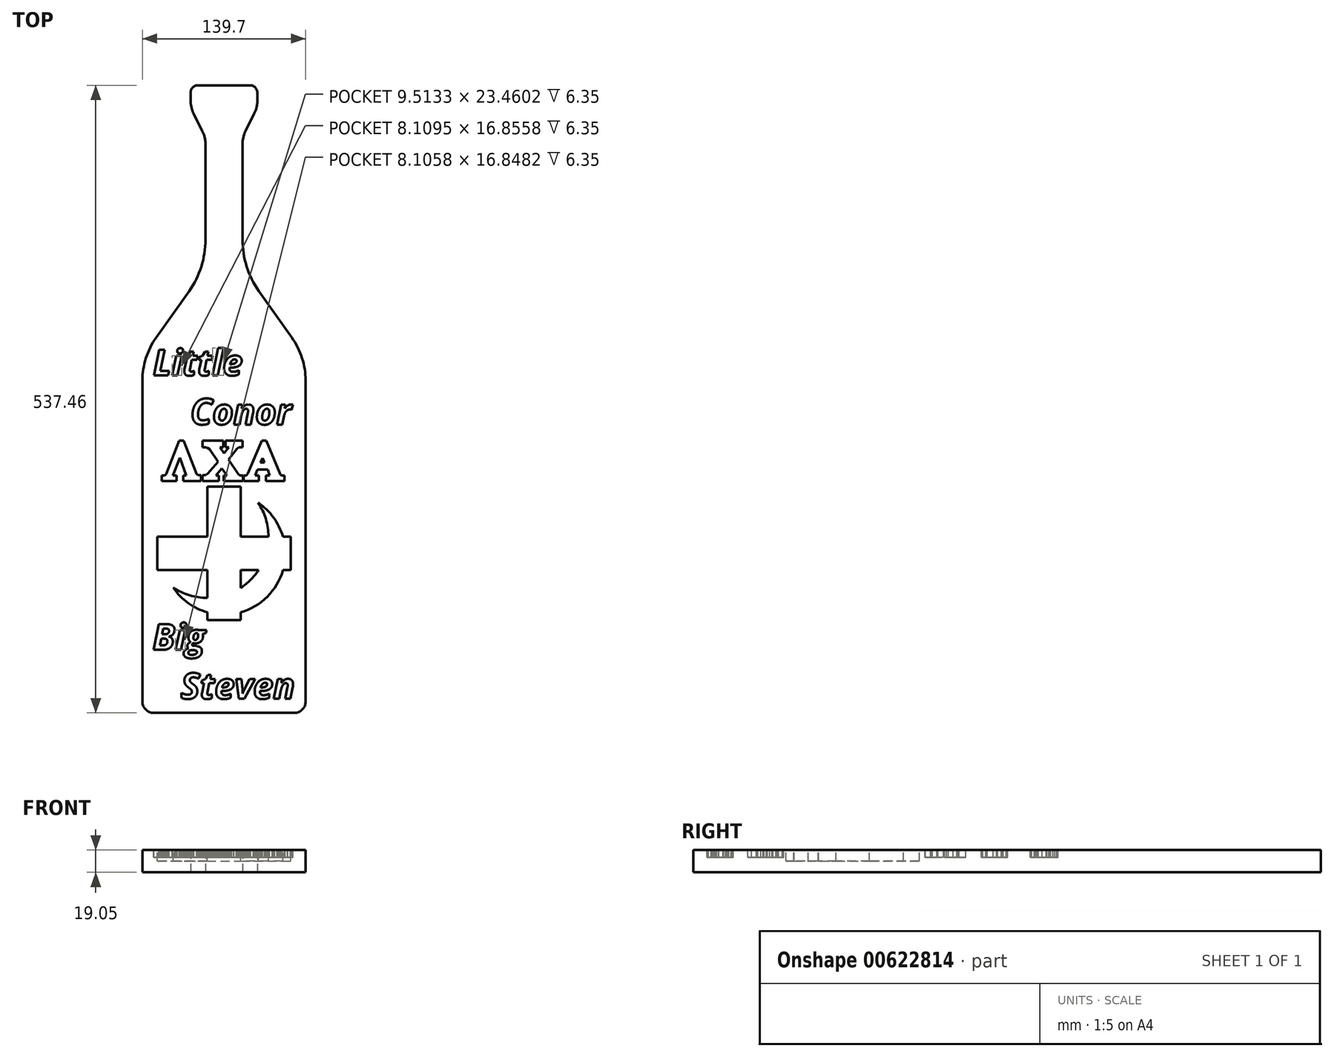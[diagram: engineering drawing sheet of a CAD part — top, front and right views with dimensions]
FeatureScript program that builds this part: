
annotation { "Feature Type Name" : "Feature", "Feature Type Description" : "" }
export const myFeature = defineFeature(function(context is Context, id is Id, definition is map)
    precondition{}
    {
        {
            var Q0;
            Q0=qCreatedBy(makeId("Top.planeOp"),FACE);
            var sketch = newSketch(context, id + "F0", { "sketchPlane" : qUnion([Q0])});
            skLineSegment(sketch, "E0", {"start": v(0, 0) * mm, "end": v(60.33, 0) * mm});
            skLineSegment(sketch, "E1", {"start": v(69.85, 9.53) * mm, "end": v(69.85, 284.59) * mm});
            skLineSegment(sketch, "E2", {"start": v(58.17, 321.3) * mm, "end": v(29.9, 361.2) * mm});
            skLineSegment(sketch, "E3", {"start": v(15.87, 405.25) * mm, "end": v(15.87, 487.01) * mm});
            skLineSegment(sketch, "E4", {"start": v(18.56, 498.37) * mm, "end": v(25.9, 513.04) * mm});
            skLineSegment(sketch, "E5", {"start": v(28.57, 524.4) * mm, "end": v(28.57, 531.1) * mm});
            skLineSegment(sketch, "E6", {"start": v(22.22, 537.46) * mm, "end": v(0, 537.46) * mm});
            skLineSegment(sketch, "E7", {"start": v(0, 537.46) * mm, "end": v(0, 0) * mm});
            skPoint(sketch, "E8.visualSharp", {"position": v(28.57, 537.46) * mm});
            skArc(sketch, "E8.filletArc", {"start": v(28.57, 531.1) * mm, "mid": v(26.72, 535.6) * mm, "end": v(22.22, 537.46) * mm});
            skPoint(sketch, "E9.visualSharp", {"position": v(28.57, 518.4) * mm});
            skArc(sketch, "E9.filletArc", {"start": v(25.9, 513.04) * mm, "mid": v(27.9, 518.57) * mm, "end": v(28.57, 524.4) * mm});
            skPoint(sketch, "E10.visualSharp", {"position": v(15.88, 493) * mm});
            skArc(sketch, "E10.filletArc", {"start": v(18.56, 498.37) * mm, "mid": v(16.55, 492.85) * mm, "end": v(15.87, 487.01) * mm});
            skPoint(sketch, "E11.visualSharp", {"position": v(15.87, 381) * mm});
            skArc(sketch, "E11.filletArc", {"start": v(15.87, 405.25) * mm, "mid": v(19.46, 382.14) * mm, "end": v(29.9, 361.2) * mm});
            skPoint(sketch, "E12.visualSharp", {"position": v(69.85, 304.8) * mm});
            skArc(sketch, "E12.filletArc", {"start": v(69.85, 284.59) * mm, "mid": v(66.86, 303.85) * mm, "end": v(58.17, 321.3) * mm});
            skPoint(sketch, "E13.visualSharp", {"position": v(69.85, 0) * mm});
            skArc(sketch, "E13.filletArc", {"start": v(60.33, 0) * mm, "mid": v(67.06, 2.79) * mm, "end": v(69.85, 9.53) * mm});
            skArc(sketch, "E14.MirrorCS", {"start": v(-25.9, 513.04) * mm, "mid": v(-27.9, 518.57) * mm, "end": v(-28.57, 524.4) * mm});
            skLineSegment(sketch, "E15.MirrorCS", {"start": v(-28.57, 524.4) * mm, "end": v(-28.57, 531.1) * mm});
            skArc(sketch, "E16.MirrorCS", {"start": v(-28.57, 531.1) * mm, "mid": v(-26.72, 535.6) * mm, "end": v(-22.22, 537.46) * mm});
            skArc(sketch, "E17.MirrorCS", {"start": v(-18.56, 498.37) * mm, "mid": v(-16.55, 492.85) * mm, "end": v(-15.87, 487.01) * mm});
            skArc(sketch, "E18.MirrorCS", {"start": v(-60.33, 0) * mm, "mid": v(-67.06, 2.79) * mm, "end": v(-69.85, 9.53) * mm});
            skLineSegment(sketch, "E19.MirrorCS", {"start": v(-18.56, 498.37) * mm, "end": v(-25.9, 513.04) * mm});
            skArc(sketch, "E20.MirrorCS", {"start": v(-69.85, 284.59) * mm, "mid": v(-66.86, 303.85) * mm, "end": v(-58.17, 321.3) * mm});
            skPoint(sketch, "E21.MirrorP", {"position": v(-69.85, 0) * mm});
            skLineSegment(sketch, "E22.MirrorCS", {"start": v(-69.85, 9.53) * mm, "end": v(-69.85, 284.59) * mm});
            skLineSegment(sketch, "E23.MirrorCS", {"start": v(-58.17, 321.3) * mm, "end": v(-29.9, 361.2) * mm});
            skLineSegment(sketch, "E24.MirrorCS", {"start": v(-15.87, 405.25) * mm, "end": v(-15.87, 487.01) * mm});
            skPoint(sketch, "E25.MirrorP", {"position": v(-69.85, 304.8) * mm});
            skPoint(sketch, "E26.MirrorP", {"position": v(-15.87, 381) * mm});
            skPoint(sketch, "E27.MirrorP", {"position": v(-28.57, 537.46) * mm});
            skArc(sketch, "E28.MirrorCS", {"start": v(-15.87, 405.25) * mm, "mid": v(-19.46, 382.14) * mm, "end": v(-29.9, 361.2) * mm});
            skPoint(sketch, "E29.MirrorP", {"position": v(-15.88, 493) * mm});
            skPoint(sketch, "E30.MirrorP", {"position": v(-28.57, 518.4) * mm});
            skLineSegment(sketch, "E31.MirrorCS", {"start": v(0, 0) * mm, "end": v(-60.33, 0) * mm});
            skLineSegment(sketch, "E32.MirrorCS", {"start": v(-22.22, 537.46) * mm, "end": v(0, 537.46) * mm});
            skSolve(sketch);
        }
        {
            var Q0;
            Q0 = qSketchRegion(id + "F0", true);
            extrude(context, id + "F1", {"entities" : qUnion([Q0]), "depth" : 19.05 * mm, "offsetDistance" : 25.4 * mm});
        }
        {
            var Q0;
            Q0=makeQuery(id+"F1.opExtrude","CAP_FACE",FACE,{"disambiguationData":[OSD([sQuery(id+"F0.wireOp",EDGE,"E0"),sQuery(id+"F0.wireOp",EDGE,"E1"),sQuery(id+"F0.wireOp",EDGE,"E2"),sQuery(id+"F0.wireOp",EDGE,"E3"),sQuery(id+"F0.wireOp",EDGE,"E4"),sQuery(id+"F0.wireOp",EDGE,"E5"),sQuery(id+"F0.wireOp",EDGE,"E6"),sQuery(id+"F0.wireOp",EDGE,"E8.filletArc"),sQuery(id+"F0.wireOp",EDGE,"E9.filletArc"),sQuery(id+"F0.wireOp",EDGE,"E10.filletArc"),sQuery(id+"F0.wireOp",EDGE,"E11.filletArc"),sQuery(id+"F0.wireOp",EDGE,"E12.filletArc"),sQuery(id+"F0.wireOp",EDGE,"E13.filletArc"),sQuery(id+"F0.wireOp",EDGE,"E14.MirrorCS"),sQuery(id+"F0.wireOp",EDGE,"E15.MirrorCS"),sQuery(id+"F0.wireOp",EDGE,"E16.MirrorCS"),sQuery(id+"F0.wireOp",EDGE,"E17.MirrorCS"),sQuery(id+"F0.wireOp",EDGE,"E18.MirrorCS"),sQuery(id+"F0.wireOp",EDGE,"E19.MirrorCS"),sQuery(id+"F0.wireOp",EDGE,"E20.MirrorCS"),sQuery(id+"F0.wireOp",EDGE,"E22.MirrorCS"),sQuery(id+"F0.wireOp",EDGE,"E23.MirrorCS"),sQuery(id+"F0.wireOp",EDGE,"E24.MirrorCS"),sQuery(id+"F0.wireOp",EDGE,"E28.MirrorCS"),sQuery(id+"F0.wireOp",EDGE,"E31.MirrorCS"),sQuery(id+"F0.wireOp",EDGE,"E32.MirrorCS")])],"isStart":false});
            var sketch = newSketch(context, id + "F2", { "sketchPlane" : qUnion([Q0])});
            skText(sketch, "E33", { "text": "Little \n    Conor", "fontName": "OpenSans-BoldItalic.ttf"});
            const initialGuessF2  = {"E33": [-0.06094, 0.28892, 1, 0, 0.02223]};
            skSetInitialGuess(sketch, initialGuessF2);
            skSolve(sketch);
        }
        {
            var Q0;
            Q0 = qSketchRegion(id + "F2", true);
            extrude(context, id + "F3", {"entities" : qUnion([Q0]), "operationType" : NewBodyOperationType.REMOVE, "oppositeDirection" : true, "depth" : 6.35 * mm, "offsetDistance" : 25.4 * mm});
        }
        {
            var Q0;
            {var subQ0=sQuery(id+"F0.wireOp",EDGE,"E23.MirrorCS");var subQ1=sQuery(id+"F0.wireOp",EDGE,"E22.MirrorCS");var subQ2=sQuery(id+"F0.wireOp",EDGE,"E20.MirrorCS");var subQ3=sQuery(id+"F0.wireOp",EDGE,"E19.MirrorCS");var subQ4=sQuery(id+"F0.wireOp",EDGE,"E18.MirrorCS");var subQ5=sQuery(id+"F0.wireOp",EDGE,"E17.MirrorCS");var subQ6=sQuery(id+"F0.wireOp",EDGE,"E16.MirrorCS");var subQ7=sQuery(id+"F0.wireOp",EDGE,"E15.MirrorCS");var subQ8=sQuery(id+"F0.wireOp",EDGE,"E14.MirrorCS");var subQ9=sQuery(id+"F0.wireOp",EDGE,"E13.filletArc");var subQ10=sQuery(id+"F0.wireOp",EDGE,"E12.filletArc");var subQ11=sQuery(id+"F0.wireOp",EDGE,"E11.filletArc");var subQ12=sQuery(id+"F0.wireOp",EDGE,"E3");var subQ13=sQuery(id+"F0.wireOp",EDGE,"E2");var subQ14=sQuery(id+"F0.wireOp",EDGE,"E1");var subQ15=sQuery(id+"F0.wireOp",EDGE,"E31.MirrorCS");var subQ16=sQuery(id+"F0.wireOp",EDGE,"E0");var subQ17=sQuery(id+"F0.wireOp",EDGE,"E4");var subQ18=sQuery(id+"F0.wireOp",EDGE,"E5");var subQ19=sQuery(id+"F0.wireOp",EDGE,"E32.MirrorCS");var subQ20=sQuery(id+"F0.wireOp",EDGE,"E6");var subQ21=sQuery(id+"F0.wireOp",EDGE,"E8.filletArc");var subQ22=sQuery(id+"F0.wireOp",EDGE,"E9.filletArc");var subQ23=sQuery(id+"F0.wireOp",EDGE,"E10.filletArc");var subQ24=sQuery(id+"F0.wireOp",EDGE,"E24.MirrorCS");var subQ25=sQuery(id+"F0.wireOp",EDGE,"E28.MirrorCS");Q0=makeQuery(id+"F3.boolean.opBoolean","SPLIT",FACE,{"disambiguationData":[TD([makeQuery(id+"F1.opExtrude","SWEPT_FACE",FACE,{"disambiguationData":[OSD([subQ14])]})])],"derivedFrom":makeQuery(id+"F1.opExtrude","CAP_FACE",FACE,{"disambiguationData":[OSD([subQ16,subQ14,subQ13,subQ12,subQ17,subQ18,subQ20,subQ21,subQ22,subQ23,subQ11,subQ10,subQ9,subQ8,subQ7,subQ6,subQ5,subQ4,subQ3,subQ2,subQ1,subQ0,subQ24,subQ25,subQ15,subQ19])],"isStart":false})});}
            var sketch = newSketch(context, id + "F4", { "sketchPlane" : qUnion([Q0])});
            skText(sketch, "E34", { "text": "Big\n   Steven", "fontName": "OpenSans-BoldItalic.ttf"});
            const initialGuessF4  = {"E34": [-0.06118, 0.05398, 1, 0, 0.02222]};
            skSetInitialGuess(sketch, initialGuessF4);
            skSolve(sketch);
        }
        {
            var Q0;
            Q0 = qSketchRegion(id + "F4", true);
            extrude(context, id + "F5", {"entities" : qUnion([Q0]), "operationType" : NewBodyOperationType.REMOVE, "oppositeDirection" : true, "depth" : 6.35 * mm, "offsetDistance" : 25.4 * mm});
        }
        {
            var Q0;
            {var subQ67=sQuery(id+"F0.wireOp",EDGE,"E28.MirrorCS");var subQ69=sQuery(id+"F0.wireOp",EDGE,"E24.MirrorCS");var subQ72=sQuery(id+"F0.wireOp",EDGE,"E10.filletArc");var subQ76=sQuery(id+"F0.wireOp",EDGE,"E9.filletArc");var subQ81=sQuery(id+"F0.wireOp",EDGE,"E8.filletArc");var subQ86=sQuery(id+"F0.wireOp",EDGE,"E32.MirrorCS");var subQ87=sQuery(id+"F0.wireOp",EDGE,"E6");var subQ92=sQuery(id+"F0.wireOp",EDGE,"E5");var subQ97=sQuery(id+"F0.wireOp",EDGE,"E4");var subQ102=sQuery(id+"F0.wireOp",EDGE,"E31.MirrorCS");var subQ103=sQuery(id+"F0.wireOp",EDGE,"E0");var subQ107=sQuery(id+"F0.wireOp",EDGE,"E1");var subQ108=makeQuery(id+"F1.opExtrude","SWEPT_FACE",FACE,{"disambiguationData":[OSD([subQ107])]});var subQ111=sQuery(id+"F0.wireOp",EDGE,"E2");var subQ114=sQuery(id+"F0.wireOp",EDGE,"E3");var subQ117=sQuery(id+"F0.wireOp",EDGE,"E11.filletArc");var subQ121=sQuery(id+"F0.wireOp",EDGE,"E12.filletArc");var subQ125=sQuery(id+"F0.wireOp",EDGE,"E13.filletArc");var subQ129=sQuery(id+"F0.wireOp",EDGE,"E14.MirrorCS");var subQ133=sQuery(id+"F0.wireOp",EDGE,"E15.MirrorCS");var subQ136=sQuery(id+"F0.wireOp",EDGE,"E16.MirrorCS");var subQ140=sQuery(id+"F0.wireOp",EDGE,"E17.MirrorCS");var subQ143=sQuery(id+"F0.wireOp",EDGE,"E18.MirrorCS");var subQ146=sQuery(id+"F0.wireOp",EDGE,"E19.MirrorCS");var subQ149=sQuery(id+"F0.wireOp",EDGE,"E20.MirrorCS");var subQ152=sQuery(id+"F0.wireOp",EDGE,"E22.MirrorCS");var subQ155=sQuery(id+"F0.wireOp",EDGE,"E23.MirrorCS");Q0=makeQuery(id+"F5.boolean.opBoolean","SPLIT",FACE,{"disambiguationData":[TD([subQ108])],"derivedFrom":makeQuery(id+"F3.boolean.opBoolean","SPLIT",FACE,{"disambiguationData":[TD([subQ108])],"derivedFrom":makeQuery(id+"F1.opExtrude","CAP_FACE",FACE,{"disambiguationData":[OSD([subQ103,subQ107,subQ111,subQ114,subQ97,subQ92,subQ87,subQ81,subQ76,subQ72,subQ117,subQ121,subQ125,subQ129,subQ133,subQ136,subQ140,subQ143,subQ146,subQ149,subQ152,subQ155,subQ69,subQ67,subQ102,subQ86])],"isStart":false})})});}
            var sketch = newSketch(context, id + "F6", { "sketchPlane" : qUnion([Q0])});
            skLineSegment(sketch, "E35", {"start": v(-38.42, 233.14) * mm, "end": v(-34.63, 233.14) * mm});
            skLineSegment(sketch, "E36", {"start": v(-34.63, 233.14) * mm, "end": v(-23.55, 204.57) * mm});
            skLineSegment(sketch, "E37", {"start": v(-23.55, 204.57) * mm, "end": v(-22.06, 203.69) * mm});
            skLineSegment(sketch, "E38", {"start": v(-22.06, 203.69) * mm, "end": v(-19.65, 203.69) * mm});
            skLineSegment(sketch, "E39", {"start": v(-19.65, 203.69) * mm, "end": v(-19.65, 198.54) * mm});
            skLineSegment(sketch, "E40", {"start": v(-19.65, 198.54) * mm, "end": v(-34.88, 198.54) * mm});
            skLineSegment(sketch, "E41", {"start": v(-34.88, 198.54) * mm, "end": v(-34.88, 203.37) * mm});
            skLineSegment(sketch, "E42", {"start": v(-34.88, 203.37) * mm, "end": v(-32.33, 203.37) * mm});
            skLineSegment(sketch, "E43", {"start": v(-32.33, 203.37) * mm, "end": v(-37.72, 218.5) * mm});
            skLineSegment(sketch, "E44", {"start": v(-37.72, 218.5) * mm, "end": v(-43.75, 203.37) * mm});
            skLineSegment(sketch, "E45", {"start": v(-43.75, 203.37) * mm, "end": v(-40.53, 203.37) * mm});
            skLineSegment(sketch, "E46", {"start": v(-40.53, 203.37) * mm, "end": v(-40.53, 198.64) * mm});
            skLineSegment(sketch, "E47", {"start": v(-40.53, 198.64) * mm, "end": v(-53.42, 198.64) * mm});
            skLineSegment(sketch, "E48", {"start": v(-53.42, 198.64) * mm, "end": v(-53.42, 203.37) * mm});
            skLineSegment(sketch, "E49", {"start": v(-53.42, 203.37) * mm, "end": v(-50.8, 203.37) * mm});
            skLineSegment(sketch, "E50", {"start": v(-50.8, 203.37) * mm, "end": v(-49.64, 204.6) * mm});
            skLineSegment(sketch, "E51", {"start": v(-49.64, 204.6) * mm, "end": v(-38.42, 233.14) * mm});
            skLineSegment(sketch, "E52", {"start": v(-18.45, 198.54) * mm, "end": v(-18.45, 203.69) * mm});
            skLineSegment(sketch, "E53", {"start": v(-18.45, 203.69) * mm, "end": v(-15.83, 203.69) * mm});
            skLineSegment(sketch, "E54", {"start": v(-15.83, 203.69) * mm, "end": v(-14, 204.75) * mm});
            skLineSegment(sketch, "E55", {"start": v(-14, 204.75) * mm, "end": v(-5.2, 215.13) * mm});
            skLineSegment(sketch, "E56", {"start": v(-5.2, 215.13) * mm, "end": v(-12.52, 225.7) * mm});
            skLineSegment(sketch, "E57", {"start": v(-12.52, 225.7) * mm, "end": v(-13.87, 226.8) * mm});
            skLineSegment(sketch, "E58", {"start": v(-13.87, 226.8) * mm, "end": v(-15.79, 227.45) * mm});
            skLineSegment(sketch, "E59", {"start": v(-15.79, 227.45) * mm, "end": v(-18.45, 227.45) * mm});
            skLineSegment(sketch, "E60", {"start": v(-0.48, 227.45) * mm, "end": v(-3.46, 227.45) * mm});
            skLineSegment(sketch, "E61", {"start": v(-3.46, 227.45) * mm, "end": v(0, 222.4) * mm});
            skLineSegment(sketch, "E62", {"start": v(0, 222.4) * mm, "end": v(4.1, 227.45) * mm});
            skLineSegment(sketch, "E63", {"start": v(4.1, 227.45) * mm, "end": v(1.22, 227.45) * mm});
            skLineSegment(sketch, "E64", {"start": v(15.99, 227.45) * mm, "end": v(12.79, 227.45) * mm});
            skLineSegment(sketch, "E65", {"start": v(12.79, 227.45) * mm, "end": v(11.44, 226.54) * mm});
            skLineSegment(sketch, "E66", {"start": v(11.44, 226.54) * mm, "end": v(10.66, 225.69) * mm});
            skLineSegment(sketch, "E67", {"start": v(10.66, 225.69) * mm, "end": v(3.78, 216.82) * mm});
            skLineSegment(sketch, "E68", {"start": v(3.78, 216.82) * mm, "end": v(12.5, 204.13) * mm});
            skLineSegment(sketch, "E69", {"start": v(12.5, 204.13) * mm, "end": v(13.23, 203.5) * mm});
            skLineSegment(sketch, "E70", {"start": v(13.23, 203.5) * mm, "end": v(14.03, 203.26) * mm});
            skLineSegment(sketch, "E71", {"start": v(14.03, 203.26) * mm, "end": v(16.12, 203.26) * mm});
            skLineSegment(sketch, "E72", {"start": v(16.12, 203.26) * mm, "end": v(16.12, 198.5) * mm});
            skLineSegment(sketch, "E73", {"start": v(16.12, 198.5) * mm, "end": v(-0.35, 198.5) * mm});
            skLineSegment(sketch, "E74", {"start": v(-0.35, 198.5) * mm, "end": v(-0.35, 203.26) * mm});
            skLineSegment(sketch, "E75", {"start": v(-0.35, 203.26) * mm, "end": v(2.43, 203.26) * mm});
            skLineSegment(sketch, "E76", {"start": v(2.43, 203.26) * mm, "end": v(-1.81, 209.44) * mm});
            skLineSegment(sketch, "E77", {"start": v(-1.81, 209.44) * mm, "end": v(-7.04, 203.26) * mm});
            skLineSegment(sketch, "E78", {"start": v(-7.04, 203.26) * mm, "end": v(-4.46, 203.26) * mm});
            skLineSegment(sketch, "E79", {"start": v(-4.46, 203.26) * mm, "end": v(-4.46, 198.5) * mm});
            skLineSegment(sketch, "E80", {"start": v(-4.46, 198.5) * mm, "end": v(-18.45, 198.54) * mm});
            skLineSegment(sketch, "E81", {"start": v(26.6, 203.26) * mm, "end": v(29.89, 203.26) * mm});
            skLineSegment(sketch, "E82", {"start": v(29.89, 203.26) * mm, "end": v(29.89, 198.54) * mm});
            skLineSegment(sketch, "E83", {"start": v(29.89, 198.54) * mm, "end": v(16.98, 198.5) * mm});
            skLineSegment(sketch, "E84", {"start": v(16.98, 198.5) * mm, "end": v(16.98, 203.26) * mm});
            skLineSegment(sketch, "E85", {"start": v(16.98, 203.26) * mm, "end": v(18.7, 203.26) * mm});
            skLineSegment(sketch, "E86", {"start": v(18.7, 203.26) * mm, "end": v(19.31, 203.69) * mm});
            skLineSegment(sketch, "E87", {"start": v(19.31, 203.69) * mm, "end": v(20.2, 204.75) * mm});
            skLineSegment(sketch, "E88", {"start": v(20.2, 204.75) * mm, "end": v(32.27, 233.14) * mm});
            skPoint(sketch, "E88.endSnap0", {"position": v(-36.52, 233.14) * mm});
            skLineSegment(sketch, "E89", {"start": v(32.27, 233.14) * mm, "end": v(36.2, 233.14) * mm});
            skLineSegment(sketch, "E90", {"start": v(36.2, 233.14) * mm, "end": v(47.87, 204.75) * mm});
            skLineSegment(sketch, "E91", {"start": v(47.87, 204.75) * mm, "end": v(48.35, 203.93) * mm});
            skLineSegment(sketch, "E92", {"start": v(48.35, 203.93) * mm, "end": v(49.4, 203.26) * mm});
            skLineSegment(sketch, "E93", {"start": v(49.4, 203.26) * mm, "end": v(51.9, 203.26) * mm});
            skLineSegment(sketch, "E94", {"start": v(51.9, 203.26) * mm, "end": v(51.92, 198.54) * mm});
            skLineSegment(sketch, "E95", {"start": v(51.92, 198.54) * mm, "end": v(36, 198.5) * mm});
            skLineSegment(sketch, "E96", {"start": v(36, 198.5) * mm, "end": v(36, 203.26) * mm});
            skLineSegment(sketch, "E97", {"start": v(36, 203.26) * mm, "end": v(39.14, 203.26) * mm});
            skLineSegment(sketch, "E98", {"start": v(39.14, 203.26) * mm, "end": v(37.33, 208.42) * mm});
            skLineSegment(sketch, "E99", {"start": v(37.33, 208.42) * mm, "end": v(28.67, 208.42) * mm});
            skLineSegment(sketch, "E100", {"start": v(28.67, 208.42) * mm, "end": v(26.6, 203.26) * mm});
            skLineSegment(sketch, "E101", {"start": v(32.93, 218.32) * mm, "end": v(31.23, 214.32) * mm});
            skLineSegment(sketch, "E102", {"start": v(32.93, 218.32) * mm, "end": v(34.58, 214.32) * mm});
            skLineSegment(sketch, "E103", {"start": v(34.58, 214.32) * mm, "end": v(31.23, 214.32) * mm});
            skLineSegment(sketch, "E104", {"start": v(-18.45, 227.45) * mm, "end": v(-18.45, 233.14) * mm});
            skPoint(sketch, "E104.endSnap0", {"position": v(34.23, 233.14) * mm});
            skLineSegment(sketch, "E105", {"start": v(-18.45, 233.14) * mm, "end": v(-0.48, 233.14) * mm});
            skLineSegment(sketch, "E106", {"start": v(-0.48, 233.14) * mm, "end": v(-0.48, 227.45) * mm});
            skLineSegment(sketch, "E107", {"start": v(1.22, 227.45) * mm, "end": v(1.22, 233.14) * mm});
            skLineSegment(sketch, "E108", {"start": v(1.22, 233.14) * mm, "end": v(15.99, 233.14) * mm});
            skLineSegment(sketch, "E109", {"start": v(15.99, 233.14) * mm, "end": v(15.99, 227.45) * mm});
            skSolve(sketch);
        }
        {
            var Q0;
            Q0=makeQuery(id+"F6.imprint","IMPRINT",FACE,{"disambiguationData":[TD([[makeQuery(id+"F6.imprint","IMPRINT",EDGE,{"derivedFrom":sQuery(id+"F6.wireOp",EDGE,"E35")}),-1.0]])]});
            var Q1;
            Q1=makeQuery(id+"F6.imprint","IMPRINT",FACE,{"disambiguationData":[TD([[makeQuery(id+"F6.imprint","IMPRINT",EDGE,{"derivedFrom":sQuery(id+"F6.wireOp",EDGE,"E52")}),-1.0]])]});
            var Q2;
            Q2=makeQuery(id+"F6.imprint","IMPRINT",FACE,{"disambiguationData":[TD([[makeQuery(id+"F6.imprint","IMPRINT",EDGE,{"derivedFrom":sQuery(id+"F6.wireOp",EDGE,"E81")}),-1.0]])]});
            extrude(context, id + "F7", {"entities" : qUnion([Q0, Q1, Q2]), "operationType" : NewBodyOperationType.REMOVE, "oppositeDirection" : true, "depth" : 6.35 * mm, "offsetDistance" : 25.4 * mm});
        }
        {
            var Q0;
            {var subQ178=sQuery(id+"F0.wireOp",EDGE,"E28.MirrorCS");var subQ180=sQuery(id+"F0.wireOp",EDGE,"E24.MirrorCS");var subQ184=sQuery(id+"F0.wireOp",EDGE,"E10.filletArc");var subQ192=sQuery(id+"F0.wireOp",EDGE,"E9.filletArc");var subQ203=sQuery(id+"F0.wireOp",EDGE,"E8.filletArc");var subQ214=sQuery(id+"F0.wireOp",EDGE,"E32.MirrorCS");var subQ215=sQuery(id+"F0.wireOp",EDGE,"E6");var subQ225=sQuery(id+"F0.wireOp",EDGE,"E5");var subQ236=sQuery(id+"F0.wireOp",EDGE,"E4");var subQ247=sQuery(id+"F0.wireOp",EDGE,"E31.MirrorCS");var subQ248=sQuery(id+"F0.wireOp",EDGE,"E0");var subQ255=sQuery(id+"F0.wireOp",EDGE,"E1");var subQ256=makeQuery(id+"F1.opExtrude","SWEPT_FACE",FACE,{"disambiguationData":[OSD([subQ255])]});var subQ262=sQuery(id+"F0.wireOp",EDGE,"E2");var subQ266=sQuery(id+"F0.wireOp",EDGE,"E3");var subQ272=sQuery(id+"F0.wireOp",EDGE,"E11.filletArc");var subQ280=sQuery(id+"F0.wireOp",EDGE,"E12.filletArc");var subQ287=sQuery(id+"F0.wireOp",EDGE,"E13.filletArc");var subQ295=sQuery(id+"F0.wireOp",EDGE,"E14.MirrorCS");var subQ302=sQuery(id+"F0.wireOp",EDGE,"E15.MirrorCS");var subQ309=sQuery(id+"F0.wireOp",EDGE,"E16.MirrorCS");var subQ316=sQuery(id+"F0.wireOp",EDGE,"E17.MirrorCS");var subQ320=sQuery(id+"F0.wireOp",EDGE,"E18.MirrorCS");var subQ324=sQuery(id+"F0.wireOp",EDGE,"E19.MirrorCS");var subQ328=sQuery(id+"F0.wireOp",EDGE,"E20.MirrorCS");var subQ332=sQuery(id+"F0.wireOp",EDGE,"E22.MirrorCS");var subQ336=sQuery(id+"F0.wireOp",EDGE,"E23.MirrorCS");Q0=makeQuery(id+"F7.boolean.opBoolean","SPLIT",FACE,{"disambiguationData":[TD([subQ256])],"derivedFrom":makeQuery(id+"F5.boolean.opBoolean","SPLIT",FACE,{"disambiguationData":[TD([subQ256])],"derivedFrom":makeQuery(id+"F3.boolean.opBoolean","SPLIT",FACE,{"disambiguationData":[TD([subQ256])],"derivedFrom":makeQuery(id+"F1.opExtrude","CAP_FACE",FACE,{"disambiguationData":[OSD([subQ248,subQ255,subQ262,subQ266,subQ236,subQ225,subQ215,subQ203,subQ192,subQ184,subQ272,subQ280,subQ287,subQ295,subQ302,subQ309,subQ316,subQ320,subQ324,subQ328,subQ332,subQ336,subQ180,subQ178,subQ247,subQ214])],"isStart":false})})})});}
            var sketch = newSketch(context, id + "F8", { "sketchPlane" : qUnion([Q0])});
            skPoint(sketch, "E110", {"position": v(0, 79.38) * mm});
            skArc(sketch, "E111", {"start": v(-43.45, 107.29) * mm, "mid": v(-29.55, 100.72) * mm, "end": v(-14.34, 98.46) * mm});
            skArc(sketch, "E112", {"start": v(-43.45, 107.29) * mm, "mid": v(-30.77, 94.13) * mm, "end": v(-14.34, 86.13) * mm});
            skLineSegment(sketch, "E113", {"start": v(-14.32, 150.83) * mm, "end": v(-57.15, 150.83) * mm});
            skLineSegment(sketch, "E114", {"start": v(-57.15, 150.83) * mm, "end": v(-57.15, 122.22) * mm});
            skLineSegment(sketch, "E115", {"start": v(-57.15, 122.22) * mm, "end": v(-14.34, 122.22) * mm});
            skLineSegment(sketch, "E116", {"start": v(-14.34, 122.22) * mm, "end": v(-14.34, 98.46) * mm});
            skLineSegment(sketch, "E117", {"start": v(-14.34, 79.38) * mm, "end": v(14.31, 79.38) * mm});
            skLineSegment(sketch, "E118", {"start": v(14.31, 79.38) * mm, "end": v(14.31, 86.1) * mm});
            skLineSegment(sketch, "E119", {"start": v(14.31, 122.22) * mm, "end": v(29.55, 122.22) * mm});
            skLineSegment(sketch, "E120", {"start": v(57.15, 122.22) * mm, "end": v(57.15, 150.88) * mm});
            skLineSegment(sketch, "E121", {"start": v(14.31, 150.88) * mm, "end": v(14.31, 193.68) * mm});
            skLineSegment(sketch, "E122", {"start": v(14.31, 193.68) * mm, "end": v(-14.34, 193.68) * mm});
            skLineSegment(sketch, "E123", {"start": v(-14.34, 193.68) * mm, "end": v(-14.32, 150.83) * mm});
            skArc(sketch, "E124.trimOffspring", {"start": v(14.31, 106.99) * mm, "mid": v(22.72, 113.81) * mm, "end": v(29.55, 122.22) * mm});
            skLineSegment(sketch, "E125.trimOffspring", {"start": v(-14.34, 86.13) * mm, "end": v(-14.34, 79.38) * mm});
            skArc(sketch, "E126.trimOffspring", {"start": v(14.31, 86.1) * mm, "mid": v(37.08, 99.46) * mm, "end": v(50.44, 122.22) * mm});
            skLineSegment(sketch, "E127.trimOffspring", {"start": v(14.31, 106.99) * mm, "end": v(14.31, 122.22) * mm});
            skLineSegment(sketch, "E128.trimOffspring", {"start": v(50.44, 122.22) * mm, "end": v(57.15, 122.22) * mm});
            skArc(sketch, "E129.trimOffspring", {"start": v(38.07, 150.88) * mm, "mid": v(35.82, 166.1) * mm, "end": v(29.24, 180) * mm});
            skArc(sketch, "E130.trimOffspring", {"start": v(50.41, 150.88) * mm, "mid": v(42.4, 167.32) * mm, "end": v(29.24, 180) * mm});
            skLineSegment(sketch, "E131.trimOffspring", {"start": v(38.07, 150.88) * mm, "end": v(14.31, 150.88) * mm});
            skLineSegment(sketch, "E132", {"start": v(50.41, 150.88) * mm, "end": v(57.15, 150.88) * mm});
            skSolve(sketch);
        }
        {
            var Q0;
            Q0 = qSketchRegion(id + "F8", true);
            extrude(context, id + "F9", {"entities" : qUnion([Q0]), "operationType" : NewBodyOperationType.REMOVE, "oppositeDirection" : true, "depth" : 9.52 * mm, "offsetDistance" : 25.4 * mm});
        }
    });
